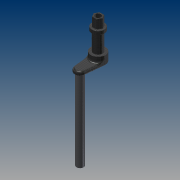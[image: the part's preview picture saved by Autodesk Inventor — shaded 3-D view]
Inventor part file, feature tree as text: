
AUTODESK INVENTOR PART (.ipt)
format: ipt  version: 2015 (Build 190159000, 159)  size: 241,664 bytes
history: native  units: mm
features: extrude x9, sketch x9, fillet x7
ambient origin geometry x8: Origin, YZ Plane, XZ Plane, XY Plane, X Axis, Y Axis, Z Axis, Center Point
bodies: Solid1 (feature_tree)
feature tree (25):
  extrude  "Extrusion1"  Depth=30.0mm TaperAngle=0.0deg
  extrude  "Extrusion2"  Depth=100.0mm TaperAngle=0.0deg
  extrude  "Extrusion3"  Depth=20.0mm TaperAngle=0.0deg
  extrude  "Extrusion4"  Depth=50.0mm TaperAngle=0.0deg
  extrude  "Extrusion5"  Depth=30.0mm
  extrude  "Extrusion6"  Depth=2.0mm
  fillet  "Fillet1"  Radius=2.0mm
  fillet  "Fillet2"  Radius=60.0mm
  extrude  "Extrusion7"  Depth=20.0mm TaperAngle=0.0deg
  fillet  "Fillet3"  Radius=10.0mm
  fillet  "Fillet4"  Radius=5.0mm
  fillet  "Fillet5"  Radius=10.0mm
  extrude  "Extrusion8"  Depth=450.0mm TaperAngle=0.0deg
  extrude  "Extrusion9"  Depth=200.0mm TaperAngle=0.0deg
  fillet  "Fillet6"  Radius=2.0mm
  fillet  "Fillet7"  Radius=5.0mm
  sketch  "Sketch1"  dims[d0=80.0mm d1=30.0mm d2=0.0mm]
  sketch  "Sketch2"  dims[d3=50.0mm d4=100.0mm d5=0.0mm]
  sketch  "Sketch3"  dims[d6=10.0mm d7=20.0mm d8=0.0mm]
  sketch  "Sketch4"  dims[d9=50.0mm d10=50.0mm d11=0.0mm]
  sketch  "Sketch5"  dims[d12=50.0mm d13=0.0mm d14=30.0mm]
  sketch  "Sketch6"  dims[d15=50.0mm d16=0.0mm d17=2.0mm d18=2.0mm d19=60.0mm]
  sketch  "Sketch7"  dims[d20=100.0mm d21=20.0mm d22=0.0mm d23=10.0mm d24=5.0mm d25=10.0mm]
  sketch  "Sketch8"  dims[d26=40.0mm d27=450.0mm d28=0.0mm]
  sketch  "Sketch9"  dims[d29=20.0mm d30=200.0mm d31=0.0mm d32=2.0mm d33=5.0mm]
